# Revit family: Gleitschlitten Typ B, höhe h=150mm, Ø500 bis Ø508mm, m.D
name_source: partatom
category: HLS-Bauteile
revit_build: Autodesk Revit 2018 (Build: 20190510_1515(x64)
units: mm (PartAtom-declared; Revit-internal decimal feet)

## family parameters
Arbeitsebenenbasiert = Ja
Beim Laden mit Abzugskörper schneiden = Nein
Bemaßung runder Anschluss = Durchmesser verwenden
Gemeinsam genutzt = Ja
Immer vertikal = Nein
Klassifizierung = Keine
Raumberechnungspunkt = Nein
Teiletyp = Normal

## types (2) — shared parameters
A (Breite) = 221 mm  [stored 0.725066 ft]
Baustoffklasse = B2
Breite Schellenband = 50 mm
Breite Unterbau = 364 mm
Dämmstärke = 6 mm  [stored 0.019685 ft]
Fabrikat = MEFA
Kurztext1 = Gleitschlitten B 50 x 5 mm
L = 310 mm  [stored 1.01706 ft]
Länge Unterbau = 390 mm
Mengeneinheit = St
Schalldämmeinlage = Gummi EPDM
Schuh = TL-Fuß für Gleitschl.2Lo.14 : 9000854
Sicherheitsfaktor = 1.54
Stärke Material = 8 mm  [stored 0.0262467 ft]
Stärke Schellenband = 5 mm
Verschluss = Schraube + Mutter
Verschluss-Schraube = M12
Vorgabe-Ansicht = 1219 mm
max. Temperaturbeständigkeit = 100 °C
vpe = 1

## per-type parameters (varying)
| type | Achshöhe | Artikelnummer | EAN | Flachmaterial | Gewicht | Gewicht pro Bauteil | Kurztext2 | RS Titan, o.D., Ø500 bis Ø508mm, 30 Grad | Rohraußendurchmesser |
| Gleitschlitten TypB, h=150mm, m.D., Ø500mm | 400 mm | 110bfb0500 | 4250928462329 | Flachmaterial nach DIN (50-5 und 70-8) : für Ø500 | 22.78 kg | 22.78 kg | 500 mm EPDM fsv | Rohrschelle Titan HD, Gummi, 30 Grad, Ø500 bis Ø508, ok : für Ø500 | 500 mm  [stored 1.64042 ft] |
| Gleitschlitten TypB, h=150mm, m.D., Ø508mm | 404 mm | 110bfb0508 | 4250928462336 | Flachmaterial nach DIN (50-5 und 70-8) : für Ø508 | 22.91 kg | 22.91 kg | 508 mm EPDM fsv | Rohrschelle Titan HD, Gummi, 30 Grad, Ø500 bis Ø508, ok : für Ø508 | 508 mm |

note: [stored X ft] marks values corroborated as IEEE doubles in the binary element streams (Revit-internal decimal feet)

## geometry (parser evidence)
native form markers: Sweep x8
no freeform markers — native parametric forms only
